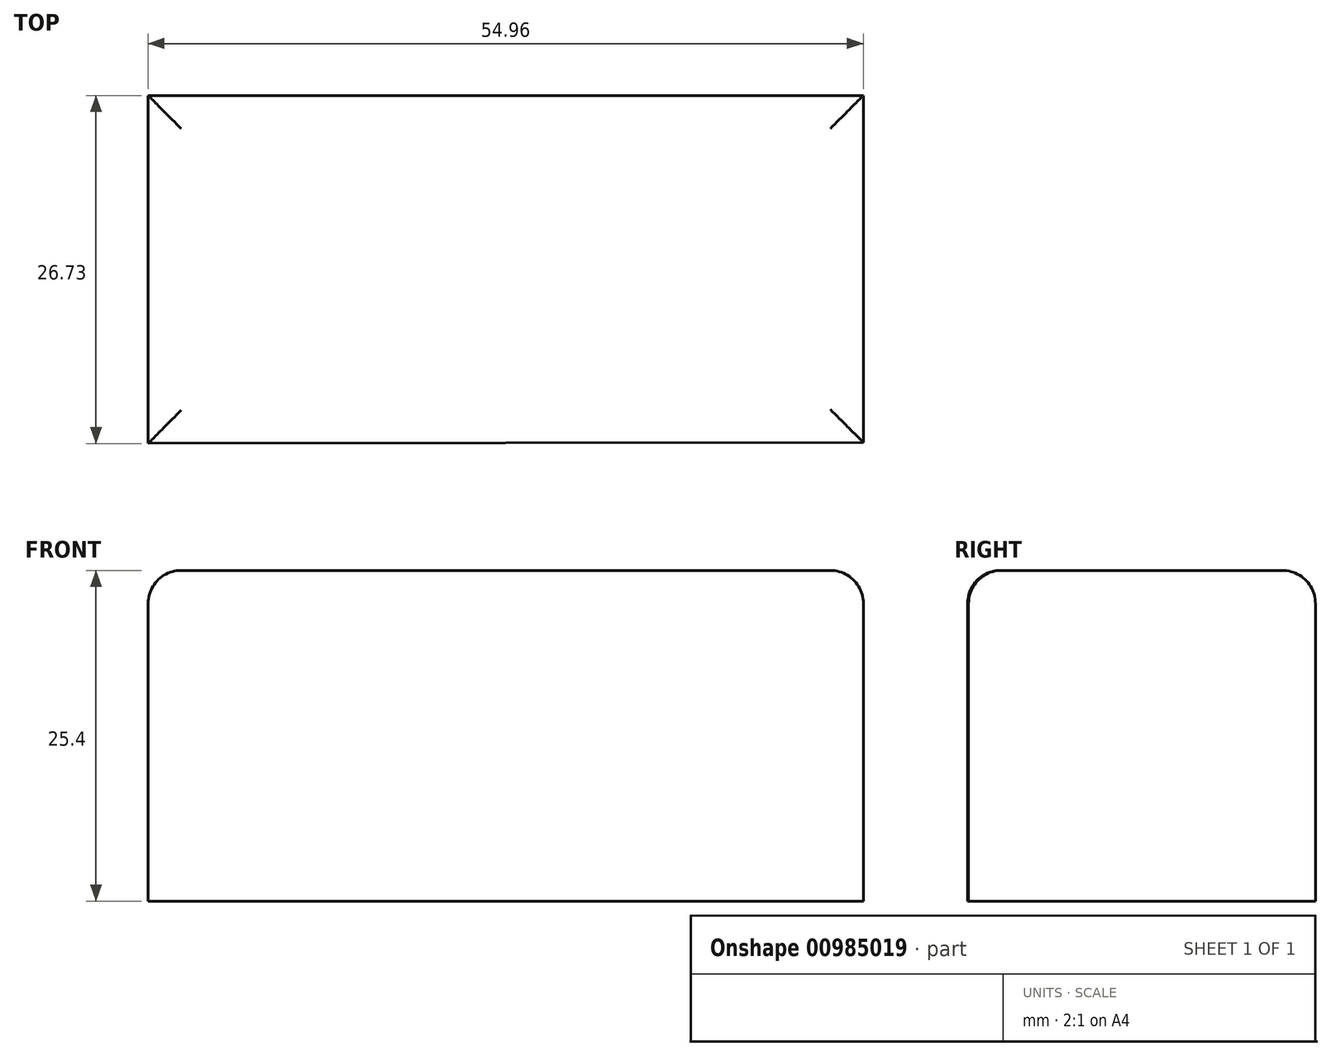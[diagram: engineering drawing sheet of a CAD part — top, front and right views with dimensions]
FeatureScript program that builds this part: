
annotation { "Feature Type Name" : "Feature", "Feature Type Description" : "" }
export const myFeature = defineFeature(function(context is Context, id is Id, definition is map)
    precondition{}
    {
        {
            var Q0;
            Q0=qCreatedBy(makeId("Top.planeOp"),FACE);
            var sketch = newSketch(context, id + "F0", { "sketchPlane" : qUnion([Q0])});
            skLineSegment(sketch, "E0", {"start": v(-30.53, 13.84) * mm, "end": v(-30.53, 0) * mm});
            skLineSegment(sketch, "E1", {"start": v(-30.53, 0) * mm, "end": v(-30.53, -12.89) * mm});
            skLineSegment(sketch, "E2", {"start": v(24.43, 13.84) * mm, "end": v(-30.53, 13.84) * mm});
            skLineSegment(sketch, "E3", {"start": v(24.43, -12.81) * mm, "end": v(24.43, 13.84) * mm});
            skLineSegment(sketch, "E4", {"start": v(24.43, -12.81) * mm, "end": v(-30.53, -12.89) * mm});
            skSolve(sketch);
        }
        {
            var Q0;
            Q0 = qSketchRegion(id + "F0", true);
            extrude(context, id + "F1", {"entities" : qUnion([Q0]), "depth" : 25.4 * mm, "offsetDistance" : 25.4 * mm});
        }
        {
            var Q0;
            Q0=makeQuery(id+"F1.opExtrude","CAP_EDGE",EDGE,{"disambiguationData":[OSD([sQuery(id+"F0.wireOp",EDGE,"E4")])],"isStart":false});
            var Q1;
            Q1=makeQuery(id+"F1.opExtrude","CAP_EDGE",EDGE,{"disambiguationData":[OSD([sQuery(id+"F0.wireOp",EDGE,"E2")])],"isStart":false});
            var Q2;
            Q2=makeQuery(id+"F1.opExtrude","CAP_EDGE",EDGE,{"disambiguationData":[OSD([sQuery(id+"F0.wireOp",EDGE,"E3")])],"isStart":false});
            var Q3;
            Q3=makeQuery(id+"F1.opExtrude","CAP_EDGE",EDGE,{"disambiguationData":[OSD([sQuery(id+"F0.wireOp",EDGE,"E0"),sQuery(id+"F0.wireOp",EDGE,"E1")])],"isStart":false});
            fillet(context, id + "F2", {"entities" : qUnion([Q0, Q1, Q2, Q3]), "radius" : 2.54 * mm, "tangentPropagation" : true, "allowEdgeOverflow" : false});
        }
    });
